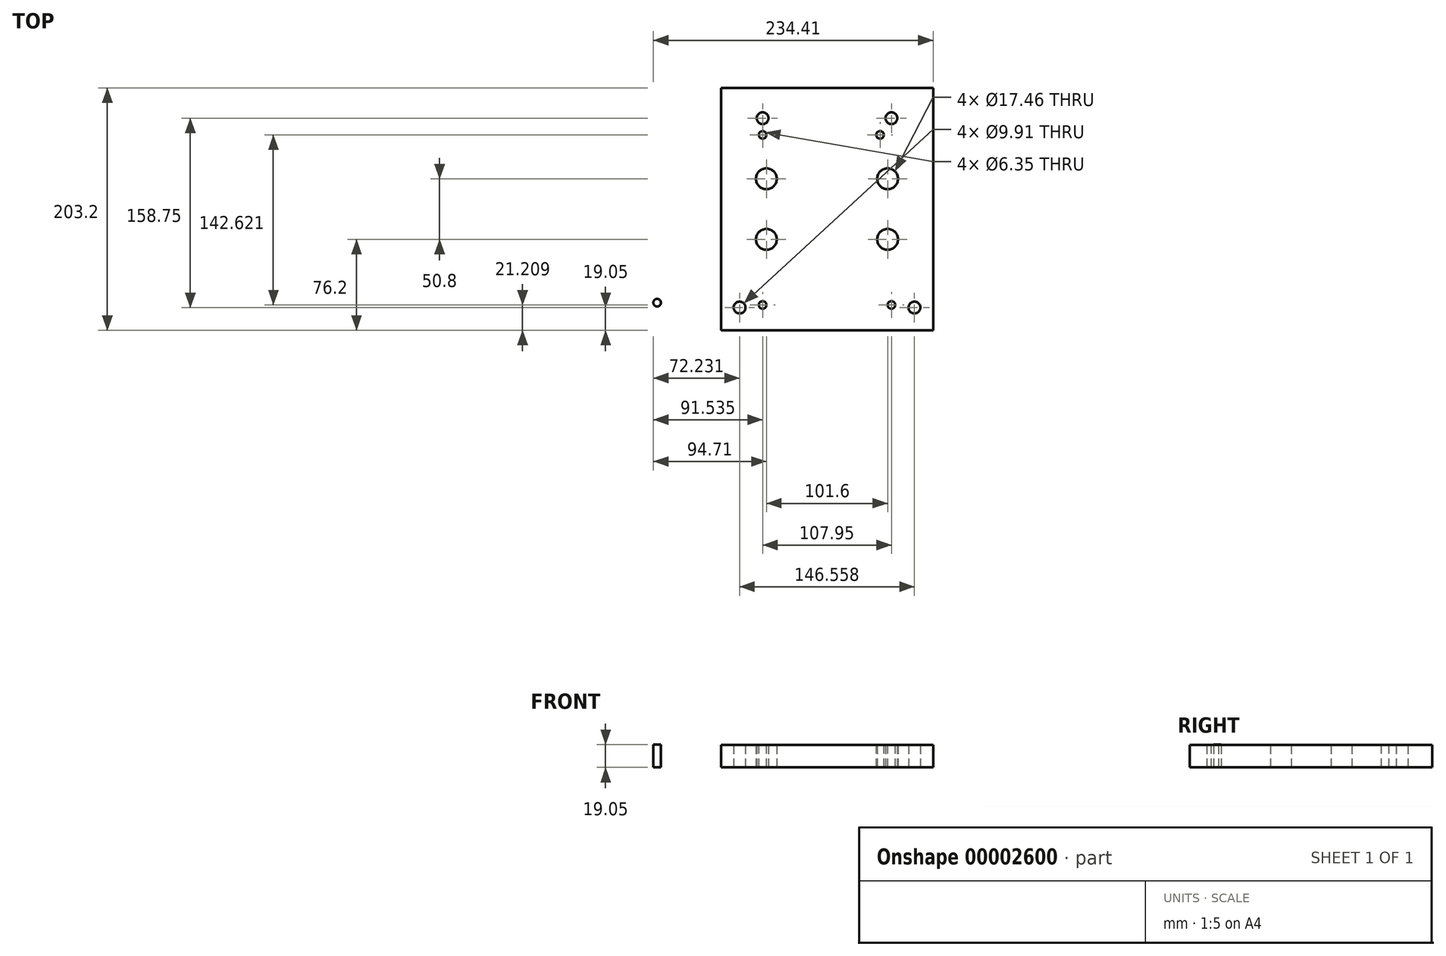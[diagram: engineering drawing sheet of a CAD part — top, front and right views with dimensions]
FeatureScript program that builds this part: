
annotation { "Feature Type Name" : "Feature", "Feature Type Description" : "" }
export const myFeature = defineFeature(function(context is Context, id is Id, definition is map)
    precondition{}
    {
        {
            var Q0;
            Q0=qCreatedBy(makeId("Top.planeOp"),FACE);
            var sketch = newSketch(context, id + "F0", { "sketchPlane" : qUnion([Q0])});
            skLineSegment(sketch, "E0.bottom", {"start": v(0, 0) * mm, "end": v(177.8, 0) * mm});
            skLineSegment(sketch, "E0.top", {"start": v(0, 203.2) * mm, "end": v(177.8, 203.2) * mm});
            skLineSegment(sketch, "E0.left", {"start": v(0, 0) * mm, "end": v(0, 203.2) * mm});
            skLineSegment(sketch, "E0.right", {"start": v(177.8, 0) * mm, "end": v(177.8, 203.2) * mm});
            skCircle(sketch, "E1", {"center": v(15.62, 19.05) * mm, "radius": 4.95 * mm});
            skCircle(sketch, "E2", {"center": v(162.18, 19.05) * mm, "radius": 4.95 * mm});
            skCircle(sketch, "E3", {"center": v(142.87, 177.8) * mm, "radius": 4.95 * mm});
            skCircle(sketch, "E4", {"center": v(34.92, 177.8) * mm, "radius": 4.95 * mm});
            skCircle(sketch, "E5", {"center": v(38.1, 127) * mm, "radius": 8.73 * mm});
            skCircle(sketch, "E6", {"center": v(139.7, 127) * mm, "radius": 8.73 * mm});
            skCircle(sketch, "E7", {"center": v(38.1, 76.2) * mm, "radius": 8.73 * mm});
            skCircle(sketch, "E8", {"center": v(139.7, 76.2) * mm, "radius": 8.73 * mm});
            skSolve(sketch);
        }
        {
            var Q0;
            Q0 = qSketchRegion(id + "F0", true);
            extrude(context, id + "F1", {"entities" : qUnion([Q0]), "depth" : 18.8 * mm});
        }
        {
            var Q0;
            Q0=makeQuery(id+"F1.opExtrude","CAP_FACE",FACE,{"disambiguationData":[OSD([sQuery(id+"F0.wireOp",EDGE,"E0.bottom"),sQuery(id+"F0.wireOp",EDGE,"E0.top"),sQuery(id+"F0.wireOp",EDGE,"E0.left"),sQuery(id+"F0.wireOp",EDGE,"E0.right"),sQuery(id+"F0.wireOp",EDGE,"E1"),sQuery(id+"F0.wireOp",EDGE,"E2"),sQuery(id+"F0.wireOp",EDGE,"E3"),sQuery(id+"F0.wireOp",EDGE,"E4"),sQuery(id+"F0.wireOp",EDGE,"E5"),sQuery(id+"F0.wireOp",EDGE,"E6"),sQuery(id+"F0.wireOp",EDGE,"E7"),sQuery(id+"F0.wireOp",EDGE,"E8")])],"isStart":false});
            var sketch = newSketch(context, id + "F2", { "sketchPlane" : qUnion([Q0])});
            skCircle(sketch, "E9", {"center": v(34.93, 21.2) * mm, "radius": 3.18 * mm});
            skCircle(sketch, "E10", {"center": v(34.92, 163.83) * mm, "radius": 3.18 * mm});
            skCircle(sketch, "E11", {"center": v(133.35, 163.83) * mm, "radius": 3.18 * mm});
            skCircle(sketch, "E12", {"center": v(142.88, 21.2) * mm, "radius": 3.18 * mm});
            skSolve(sketch);
        }
        {
            var Q0;
            Q0 = qSketchRegion(id + "F2", true);
            extrude(context, id + "F3", {"entities" : qUnion([Q0]), "operationType" : NewBodyOperationType.REMOVE, "endBound" : BoundingType.THROUGH_ALL, "oppositeDirection" : true, "depth" : 25.4 * mm});
        }
        {
            var Q0;
            Q0=qCreatedBy(makeId("Top.planeOp"),FACE);
            var sketch = newSketch(context, id + "F4", { "sketchPlane" : qUnion([Q0])});
            skCircle(sketch, "E13", {"center": v(-53.43, 23.12) * mm, "radius": 3.18 * mm});
            skSolve(sketch);
        }
        {
            var Q0;
            Q0 = qSketchRegion(id + "F4", true);
            extrude(context, id + "F5", {"entities" : qUnion([Q0]), "depth" : 19.05 * mm});
        }
    });
